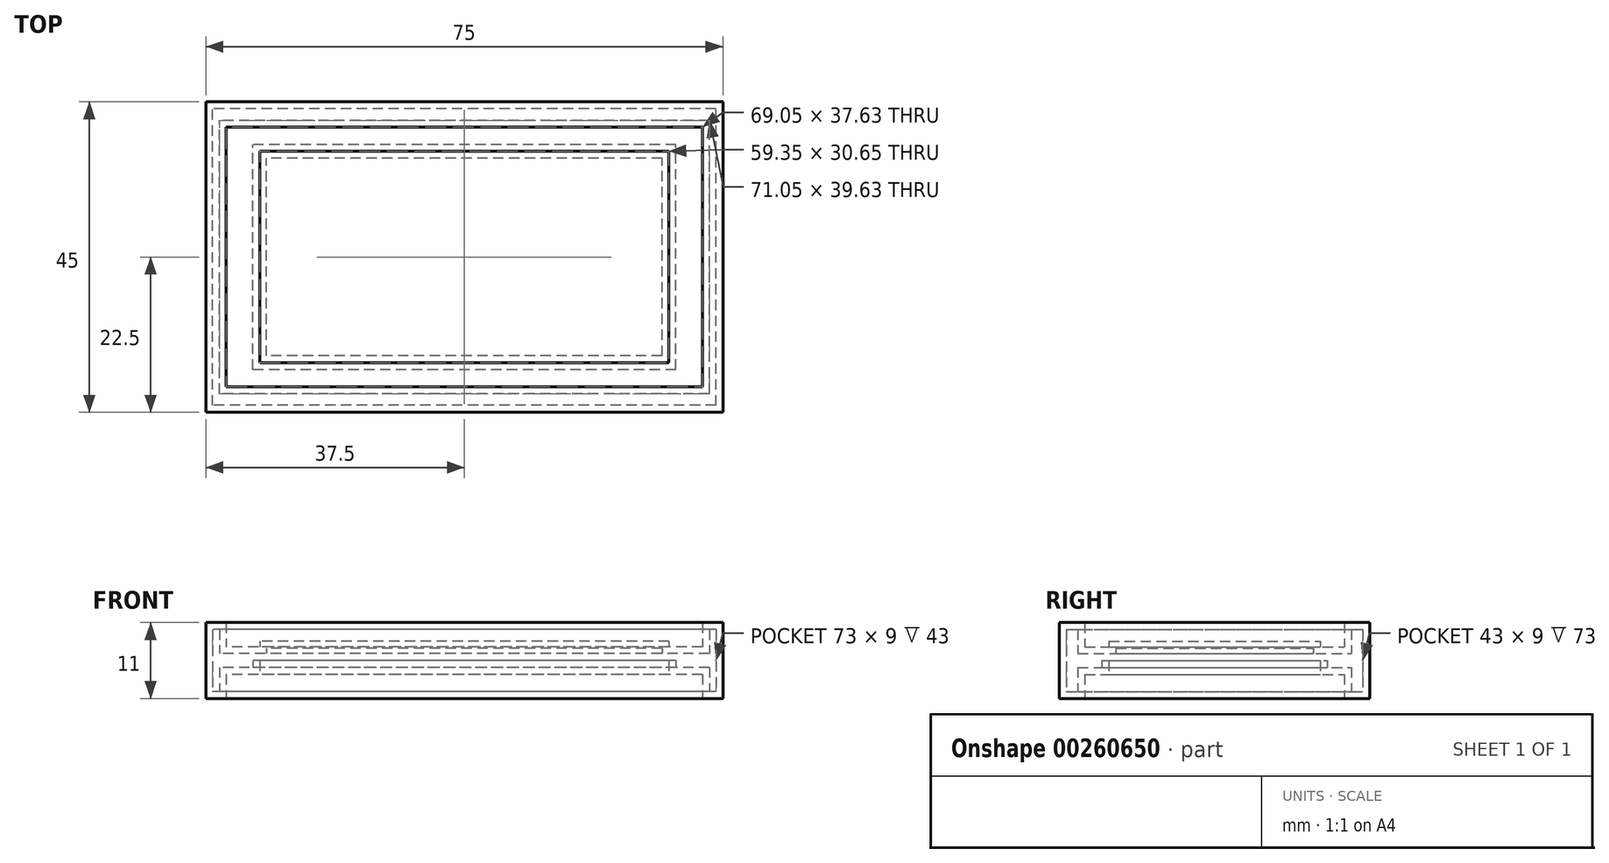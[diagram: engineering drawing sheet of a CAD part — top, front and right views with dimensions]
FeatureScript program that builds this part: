
annotation { "Feature Type Name" : "Feature", "Feature Type Description" : "" }
export const myFeature = defineFeature(function(context is Context, id is Id, definition is map)
    precondition{}
    {
        {
            var Q0;
            Q0=qCreatedBy(makeId("Top.planeOp"),FACE);
            var sketch = newSketch(context, id + "F0", { "sketchPlane" : qUnion([Q0])});
            skLineSegment(sketch, "E0.bottom", {"start": v(37.5, -22.5) * mm, "end": v(-37.5, -22.5) * mm});
            skLineSegment(sketch, "E0.top", {"start": v(37.5, 22.5) * mm, "end": v(-37.5, 22.5) * mm});
            skLineSegment(sketch, "E0.left", {"start": v(37.5, -22.5) * mm, "end": v(37.5, 22.5) * mm});
            skLineSegment(sketch, "E0.right", {"start": v(-37.5, -22.5) * mm, "end": v(-37.5, 22.5) * mm});
            skPoint(sketch, "E0.middle", {"position": v(0, 0) * mm});
            skLineSegment(sketch, "E1.bottom", {"start": v(34.53, -18.81) * mm, "end": v(-34.53, -18.81) * mm});
            skLineSegment(sketch, "E1.top", {"start": v(34.53, 18.81) * mm, "end": v(-34.53, 18.81) * mm});
            skLineSegment(sketch, "E1.left", {"start": v(34.53, -18.81) * mm, "end": v(34.53, 18.81) * mm});
            skLineSegment(sketch, "E1.right", {"start": v(-34.53, -18.81) * mm, "end": v(-34.53, 18.81) * mm});
            skLineSegment(sketch, "E2.bottom", {"start": v(29.68, -15.32) * mm, "end": v(-29.68, -15.32) * mm});
            skLineSegment(sketch, "E2.top", {"start": v(29.68, 15.32) * mm, "end": v(-29.68, 15.32) * mm});
            skLineSegment(sketch, "E2.left", {"start": v(29.68, -15.32) * mm, "end": v(29.68, 15.32) * mm});
            skLineSegment(sketch, "E2.right", {"start": v(-29.68, -15.32) * mm, "end": v(-29.68, 15.32) * mm});
            skSolve(sketch);
        }
        {
            var Q0;
            Q0 = qSketchRegion(id + "F0", true);
            extrude(context, id + "F1", {"entities" : qUnion([Q0]), "endBound" : BoundingType.SYMMETRIC, "depth" : 11 * mm});
        }
        {
            var Q0;
            Q0=makeQuery(id+"F0.imprint","IMPRINT",FACE,{"disambiguationData":[TD([[makeQuery(id+"F0.imprint","IMPRINT",EDGE,{"derivedFrom":sQuery(id+"F0.wireOp",EDGE,"E1.bottom")}),-1.0]])]});
            extrude(context, id + "F2", {"entities" : qUnion([Q0]), "operationType" : NewBodyOperationType.ADD, "endBound" : BoundingType.SYMMETRIC, "depth" : 4 * mm});
        }
        {
            var Q0;
            Q0=makeQuery(id+"F0.imprint","IMPRINT",FACE,{"disambiguationData":[TD([[makeQuery(id+"F0.imprint","IMPRINT",EDGE,{"derivedFrom":sQuery(id+"F0.wireOp",EDGE,"E2.bottom")}),-1.0]])]});
            extrude(context, id + "F3", {"entities" : qUnion([Q0]), "operationType" : NewBodyOperationType.ADD, "depth" : 2.8 * mm});
        }
        {
            var Q0;
            Q0=makeQuery(id+"F3.opExtrude","CAP_FACE",FACE,{"disambiguationData":[OSD([sQuery(id+"F0.wireOp",EDGE,"E2.bottom"),sQuery(id+"F0.wireOp",EDGE,"E2.top"),sQuery(id+"F0.wireOp",EDGE,"E2.left"),sQuery(id+"F0.wireOp",EDGE,"E2.right")])],"isStart":true});
            shell(context, id + "F4", {"entities" : qUnion([Q0]), "thickness" : 1 * mm});
        }
    });
